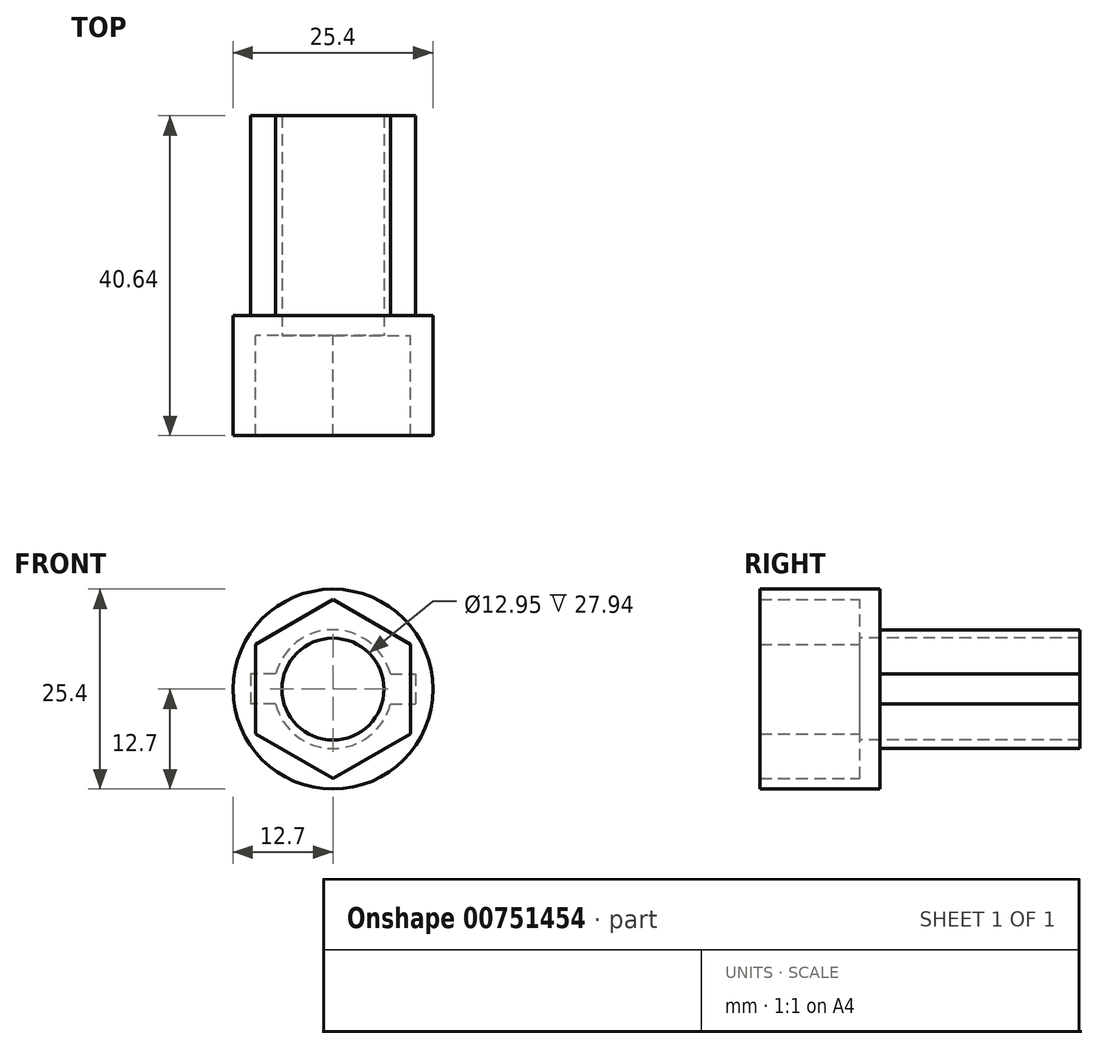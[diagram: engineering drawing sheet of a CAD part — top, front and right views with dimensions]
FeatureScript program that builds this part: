
annotation { "Feature Type Name" : "Feature", "Feature Type Description" : "" }
export const myFeature = defineFeature(function(context is Context, id is Id, definition is map)
    precondition{}
    {
        {
            var Q0;
            Q0=qCreatedBy(makeId("Front.planeOp"),FACE);
            var sketch = newSketch(context, id + "F0", { "sketchPlane" : qUnion([Q0])});
            skCircle(sketch, "E0", {"center": v(0, 0) * mm, "radius": 7.54 * mm});
            skLineSegment(sketch, "E1.bottom", {"start": v(7.3, 1.9) * mm, "end": v(10.47, 1.9) * mm});
            skLineSegment(sketch, "E1.top", {"start": v(7.3, -1.9) * mm, "end": v(10.47, -1.9) * mm});
            skLineSegment(sketch, "E1.left", {"start": v(7.3, 1.9) * mm, "end": v(7.3, -1.9) * mm});
            skLineSegment(sketch, "E1.right", {"start": v(10.47, 1.9) * mm, "end": v(10.47, -1.9) * mm});
            skLineSegment(sketch, "E2.bottom", {"start": v(-7.3, 1.9) * mm, "end": v(-10.47, 1.9) * mm});
            skLineSegment(sketch, "E2.top", {"start": v(-7.3, -1.9) * mm, "end": v(-10.47, -1.9) * mm});
            skLineSegment(sketch, "E2.left", {"start": v(-7.3, 1.9) * mm, "end": v(-7.3, -1.9) * mm});
            skLineSegment(sketch, "E2.right", {"start": v(-10.47, 1.9) * mm, "end": v(-10.47, -1.9) * mm});
            skCircle(sketch, "E3", {"center": v(0, 0) * mm, "radius": 6.48 * mm});
            skCircle(sketch, "E4.cCircle", {"center": v(0, 0) * mm, "radius": 9.84 * mm, "construction": true});
            skLineSegment(sketch, "E4.0", {"start": v(9.84, 5.68) * mm, "end": v(9.84, -5.68) * mm});
            skLineSegment(sketch, "E4.1", {"start": v(9.84, -5.68) * mm, "end": v(0, -11.37) * mm});
            skLineSegment(sketch, "E4.2", {"start": v(0, -11.37) * mm, "end": v(-9.84, -5.68) * mm});
            skLineSegment(sketch, "E4.3", {"start": v(-9.84, -5.68) * mm, "end": v(-9.84, 5.68) * mm});
            skLineSegment(sketch, "E4.4", {"start": v(-9.84, 5.68) * mm, "end": v(0, 11.37) * mm});
            skLineSegment(sketch, "E4.5", {"start": v(0, 11.37) * mm, "end": v(9.84, 5.68) * mm});
            skPoint(sketch, "E4.0.midPoint", {"position": v(9.84, 0) * mm});
            skCircle(sketch, "E5", {"center": v(0, 0) * mm, "radius": 12.7 * mm});
            skSolve(sketch);
        }
        {
            var Q0;
            {var subQ0=sQuery(id+"F0.wireOp",EDGE,"E5");var subQ1=sQuery(id+"F0.wireOp",EDGE,"E4.2");var subQ2=makeQuery(id+"F0.imprint","INTERSECT",VERTEX,{"disambiguationData":[OD(0.0)],"derivedFrom":[subQ1,subQ0]});Q0=makeQuery(id+"F0.imprint","IMPRINT",FACE,{"disambiguationData":[TD([[makeQuery(id+"F0.imprint","IMPRINT",EDGE,{"disambiguationData":[TD([[subQ2,-1.0]])],"derivedFrom":subQ1}),1.0]])]});}
            var Q1;
            {var subQ0=sQuery(id+"F0.wireOp",EDGE,"E5");var subQ1=sQuery(id+"F0.wireOp",EDGE,"E4.1");var subQ2=makeQuery(id+"F0.imprint","INTERSECT",VERTEX,{"disambiguationData":[OD(0.0)],"derivedFrom":[subQ1,subQ0]});Q1=makeQuery(id+"F0.imprint","IMPRINT",FACE,{"disambiguationData":[TD([[makeQuery(id+"F0.imprint","IMPRINT",EDGE,{"disambiguationData":[TD([[subQ2,-1.0]])],"derivedFrom":subQ1}),1.0]])]});}
            var Q2;
            {var subQ5=sQuery(id+"F0.wireOp",EDGE,"E1.right");Q2=makeQuery(id+"F0.imprint","IMPRINT",FACE,{"disambiguationData":[TD([[makeQuery(id+"F0.imprint","IMPRINT",EDGE,{"derivedFrom":subQ5}),1.0]])]});}
            var Q3;
            {var subQ0=sQuery(id+"F0.wireOp",EDGE,"E1.right");Q3=makeQuery(id+"F0.imprint","IMPRINT",FACE,{"disambiguationData":[TD([[makeQuery(id+"F0.imprint","IMPRINT",EDGE,{"derivedFrom":subQ0}),-1.0]])]});}
            var Q4;
            {var subQ0=sQuery(id+"F0.wireOp",EDGE,"E5");var subQ1=sQuery(id+"F0.wireOp",EDGE,"E4.5");var subQ2=makeQuery(id+"F0.imprint","INTERSECT",VERTEX,{"disambiguationData":[OD(0.0)],"derivedFrom":[subQ1,subQ0]});Q4=makeQuery(id+"F0.imprint","IMPRINT",FACE,{"disambiguationData":[TD([[makeQuery(id+"F0.imprint","IMPRINT",EDGE,{"disambiguationData":[TD([[subQ2,-1.0]])],"derivedFrom":subQ1}),1.0]])]});}
            var Q5;
            {var subQ0=sQuery(id+"F0.wireOp",EDGE,"E5");var subQ1=sQuery(id+"F0.wireOp",EDGE,"E4.4");var subQ2=makeQuery(id+"F0.imprint","INTERSECT",VERTEX,{"disambiguationData":[OD(0.0)],"derivedFrom":[subQ1,subQ0]});Q5=makeQuery(id+"F0.imprint","IMPRINT",FACE,{"disambiguationData":[TD([[makeQuery(id+"F0.imprint","IMPRINT",EDGE,{"disambiguationData":[TD([[subQ2,-1.0]])],"derivedFrom":subQ1}),1.0]])]});}
            var Q6;
            {var subQ5=sQuery(id+"F0.wireOp",EDGE,"E2.right");Q6=makeQuery(id+"F0.imprint","IMPRINT",FACE,{"disambiguationData":[TD([[makeQuery(id+"F0.imprint","IMPRINT",EDGE,{"derivedFrom":subQ5}),-1.0]])]});}
            var Q7;
            {var subQ0=sQuery(id+"F0.wireOp",EDGE,"E2.right");Q7=makeQuery(id+"F0.imprint","IMPRINT",FACE,{"disambiguationData":[TD([[makeQuery(id+"F0.imprint","IMPRINT",EDGE,{"derivedFrom":subQ0}),1.0]])]});}
            extrude(context, id + "F1", {"entities" : qUnion([Q0, Q1, Q2, Q3, Q4, Q5, Q6, Q7]), "depth" : 12.7 * mm, "offsetDistance" : 25.4 * mm});
        }
        {
            var Q0;
            {var subQ0=sQuery(id+"F0.wireOp",EDGE,"E5");var subQ1=sQuery(id+"F0.wireOp",EDGE,"E4.4");var subQ2=makeQuery(id+"F0.imprint","INTERSECT",VERTEX,{"disambiguationData":[OD(0.0)],"derivedFrom":[subQ1,subQ0]});Q0=makeQuery(id+"F0.imprint","IMPRINT",FACE,{"disambiguationData":[TD([[makeQuery(id+"F0.imprint","IMPRINT",EDGE,{"disambiguationData":[TD([[subQ2,-1.0]])],"derivedFrom":subQ1}),1.0]])]});}
            var Q1;
            {var subQ0=sQuery(id+"F0.wireOp",EDGE,"E5");var subQ1=sQuery(id+"F0.wireOp",EDGE,"E4.5");var subQ2=makeQuery(id+"F0.imprint","INTERSECT",VERTEX,{"disambiguationData":[OD(0.0)],"derivedFrom":[subQ1,subQ0]});Q1=makeQuery(id+"F0.imprint","IMPRINT",FACE,{"disambiguationData":[TD([[makeQuery(id+"F0.imprint","IMPRINT",EDGE,{"disambiguationData":[TD([[subQ2,-1.0]])],"derivedFrom":subQ1}),1.0]])]});}
            var Q2;
            {var subQ5=sQuery(id+"F0.wireOp",EDGE,"E1.right");Q2=makeQuery(id+"F0.imprint","IMPRINT",FACE,{"disambiguationData":[TD([[makeQuery(id+"F0.imprint","IMPRINT",EDGE,{"derivedFrom":subQ5}),1.0]])]});}
            var Q3;
            {var subQ0=sQuery(id+"F0.wireOp",EDGE,"E5");var subQ1=sQuery(id+"F0.wireOp",EDGE,"E4.1");var subQ2=makeQuery(id+"F0.imprint","INTERSECT",VERTEX,{"disambiguationData":[OD(0.0)],"derivedFrom":[subQ1,subQ0]});Q3=makeQuery(id+"F0.imprint","IMPRINT",FACE,{"disambiguationData":[TD([[makeQuery(id+"F0.imprint","IMPRINT",EDGE,{"disambiguationData":[TD([[subQ2,-1.0]])],"derivedFrom":subQ1}),1.0]])]});}
            var Q4;
            {var subQ0=sQuery(id+"F0.wireOp",EDGE,"E5");var subQ1=sQuery(id+"F0.wireOp",EDGE,"E4.2");var subQ2=makeQuery(id+"F0.imprint","INTERSECT",VERTEX,{"disambiguationData":[OD(0.0)],"derivedFrom":[subQ1,subQ0]});Q4=makeQuery(id+"F0.imprint","IMPRINT",FACE,{"disambiguationData":[TD([[makeQuery(id+"F0.imprint","IMPRINT",EDGE,{"disambiguationData":[TD([[subQ2,-1.0]])],"derivedFrom":subQ1}),1.0]])]});}
            var Q5;
            {var subQ5=sQuery(id+"F0.wireOp",EDGE,"E2.right");Q5=makeQuery(id+"F0.imprint","IMPRINT",FACE,{"disambiguationData":[TD([[makeQuery(id+"F0.imprint","IMPRINT",EDGE,{"derivedFrom":subQ5}),-1.0]])]});}
            var Q6;
            {var subQ10=sQuery(id+"F0.wireOp",EDGE,"E4.4");Q6=makeQuery(id+"F0.imprint","IMPRINT",FACE,{"disambiguationData":[TD([[makeQuery(id+"F0.imprint","IMPRINT",EDGE,{"derivedFrom":subQ10}),-1.0]])]});}
            var Q7;
            {var subQ0=sQuery(id+"F0.wireOp",EDGE,"E4.1");Q7=makeQuery(id+"F0.imprint","IMPRINT",FACE,{"disambiguationData":[TD([[makeQuery(id+"F0.imprint","IMPRINT",EDGE,{"derivedFrom":subQ0}),-1.0]])]});}
            extrude(context, id + "F2", {"entities" : qUnion([Q0, Q1, Q2, Q3, Q4, Q5, Q6, Q7]), "operationType" : NewBodyOperationType.ADD, "oppositeDirection" : true, "depth" : 2.54 * mm, "offsetDistance" : 25.4 * mm});
        }
        {
            var Q0;
            {var subQ1=sQuery(id+"F0.wireOp",EDGE,"E1.bottom");var subQ6=sQuery(id+"F0.wireOp",EDGE,"E4.0");var subQ7=makeQuery(id+"F0.imprint","INTERSECT",VERTEX,{"derivedFrom":[subQ1,subQ6]});Q0=makeQuery(id+"F0.imprint","IMPRINT",FACE,{"disambiguationData":[TD([[makeQuery(id+"F0.imprint","IMPRINT",EDGE,{"disambiguationData":[TD([[subQ7,-1.0]])],"derivedFrom":subQ6}),-1.0]])]});}
            var Q1;
            {var subQ0=sQuery(id+"F0.wireOp",EDGE,"E1.left");Q1=makeQuery(id+"F0.imprint","IMPRINT",FACE,{"disambiguationData":[TD([[makeQuery(id+"F0.imprint","IMPRINT",EDGE,{"derivedFrom":subQ0}),1.0]])]});}
            var Q2;
            {var subQ1=sQuery(id+"F0.wireOp",EDGE,"E1.left");Q2=makeQuery(id+"F0.imprint","IMPRINT",FACE,{"disambiguationData":[TD([[makeQuery(id+"F0.imprint","IMPRINT",EDGE,{"derivedFrom":subQ1}),-1.0]])]});}
            var Q3;
            {var subQ0=sQuery(id+"F0.wireOp",EDGE,"E2.left");Q3=makeQuery(id+"F0.imprint","IMPRINT",FACE,{"disambiguationData":[TD([[makeQuery(id+"F0.imprint","IMPRINT",EDGE,{"derivedFrom":subQ0}),-1.0]])]});}
            var Q4;
            {var subQ1=sQuery(id+"F0.wireOp",EDGE,"E2.bottom");var subQ6=sQuery(id+"F0.wireOp",EDGE,"E4.3");var subQ7=makeQuery(id+"F0.imprint","INTERSECT",VERTEX,{"derivedFrom":[subQ1,subQ6]});Q4=makeQuery(id+"F0.imprint","IMPRINT",FACE,{"disambiguationData":[TD([[makeQuery(id+"F0.imprint","IMPRINT",EDGE,{"disambiguationData":[TD([[subQ7,1.0]])],"derivedFrom":subQ6}),-1.0]])]});}
            var Q5;
            {var subQ0=sQuery(id+"F0.wireOp",EDGE,"E1.right");Q5=makeQuery(id+"F0.imprint","IMPRINT",FACE,{"disambiguationData":[TD([[makeQuery(id+"F0.imprint","IMPRINT",EDGE,{"derivedFrom":subQ0}),-1.0]])]});}
            var Q6;
            {var subQ0=sQuery(id+"F0.wireOp",EDGE,"E2.right");Q6=makeQuery(id+"F0.imprint","IMPRINT",FACE,{"disambiguationData":[TD([[makeQuery(id+"F0.imprint","IMPRINT",EDGE,{"derivedFrom":subQ0}),1.0]])]});}
            extrude(context, id + "F3", {"entities" : qUnion([Q0, Q1, Q2, Q3, Q4, Q5, Q6]), "operationType" : NewBodyOperationType.ADD, "oppositeDirection" : true, "depth" : 27.94 * mm, "offsetDistance" : 25.4 * mm});
        }
    });
